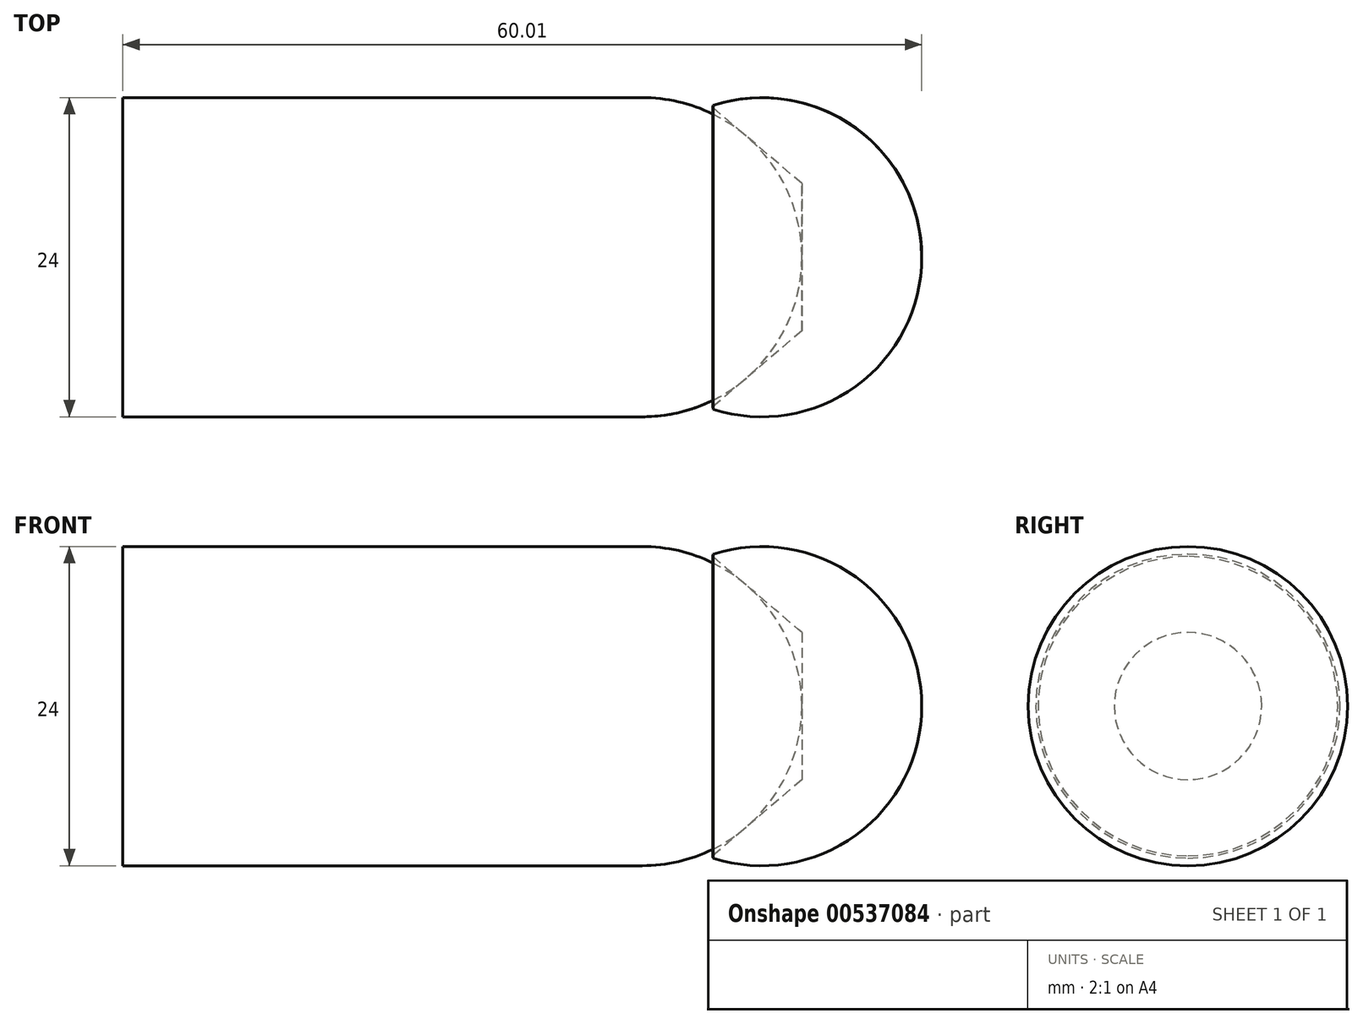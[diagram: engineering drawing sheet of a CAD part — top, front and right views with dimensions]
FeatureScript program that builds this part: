
annotation { "Feature Type Name" : "Feature", "Feature Type Description" : "" }
export const myFeature = defineFeature(function(context is Context, id is Id, definition is map)
    precondition{}
    {
        {
            var Q0;
            Q0=qCreatedBy(makeId("Top.planeOp"),FACE);
            var sketch = newSketch(context, id + "F0", { "sketchPlane" : qUnion([Q0])});
            skCircle(sketch, "E0", {"center": v(0, 0) * mm, "radius": 12 * mm});
            skCircle(sketch, "E1", {"center": v(9, 0) * mm, "radius": 12 * mm});
            skLineSegment(sketch, "E2", {"start": v(0, 12) * mm, "end": v(-39.01, 12) * mm});
            skLineSegment(sketch, "E3", {"start": v(-39.01, 12) * mm, "end": v(-39.01, -12) * mm});
            skLineSegment(sketch, "E4", {"start": v(-39.01, -12) * mm, "end": v(0, -12) * mm});
            skLineSegment(sketch, "E5", {"start": v(-39.01, 0) * mm, "end": v(36, 0) * mm});
            skLineSegment(sketch, "E6", {"start": v(5.16, 11.37) * mm, "end": v(12, 5.53) * mm});
            skLineSegment(sketch, "E7", {"start": v(12, 5.53) * mm, "end": v(12, 0) * mm});
            skSolve(sketch);
        }
        {
            var Q0;
            {var subQ0=sQuery(id+"F0.wireOp",EDGE,"E2");Q0=makeQuery(id+"F0.imprint","IMPRINT",FACE,{"disambiguationData":[TD([[makeQuery(id+"F0.imprint","IMPRINT",EDGE,{"derivedFrom":subQ0}),1.0]])]});}
            var Q1;
            {var subQ0=sQuery(id+"F0.wireOp",EDGE,"E0");var subQ1=makeQuery(id+"F0.imprint","INTERSECT",VERTEX,{"derivedFrom":[subQ0,sQuery(id+"F0.wireOp",EDGE,"E2")]});Q1=makeQuery(id+"F0.imprint","IMPRINT",FACE,{"disambiguationData":[TD([[makeQuery(id+"F0.imprint","IMPRINT",EDGE,{"disambiguationData":[TD([[subQ1,1.0]])],"derivedFrom":subQ0}),1.0]])]});}
            var Q2;
            {var subQ0=sQuery(id+"F0.wireOp",EDGE,"E1");var subQ1=sQuery(id+"F0.wireOp",EDGE,"E0");var subQ2=makeQuery(id+"F0.imprint","INTERSECT",VERTEX,{"disambiguationData":[OD(0.0)],"derivedFrom":[subQ1,subQ0]});Q2=makeQuery(id+"F0.imprint","IMPRINT",FACE,{"disambiguationData":[TD([[makeQuery(id+"F0.imprint","IMPRINT",EDGE,{"disambiguationData":[TD([[subQ2,-1.0]])],"derivedFrom":subQ0}),1.0]])]});}
            var Q3;
            Q3=sQuery(id+"F0.wireOp",EDGE,"E5");
            revolve(context, id + "F1", {"entities" : qUnion([Q0, Q1, Q2]), "axis" : qUnion([Q3]), "revolveType" : RevolveType.FULL, "oppositeDirection" : true});
        }
        {
            var Q0;
            {var subQ0=sQuery(id+"F0.wireOp",EDGE,"E7");Q0=makeQuery(id+"F0.imprint","IMPRINT",FACE,{"disambiguationData":[TD([[makeQuery(id+"F0.imprint","IMPRINT",EDGE,{"derivedFrom":subQ0}),1.0]])]});}
            var Q1;
            Q1=sQuery(id+"F0.wireOp",EDGE,"E5");
            revolve(context, id + "F2", {"entities" : qUnion([Q0]), "axis" : qUnion([Q1]), "revolveType" : RevolveType.FULL});
        }
        {
            var Q0;
            Q0=makeQuery(id+"F2.opRevolve","SWEPT_EDGE",EDGE,{"disambiguationData":[OSD([sQuery(id+"F0.wireOp",EDGE,"E1"),sQuery(id+"F0.wireOp",EDGE,"E6")])]});
            chamfer(context, id + "F3", {"entities" : qUnion([Q0]), "width" : .1 * mm, "tangentPropagation" : true});
        }
    });
